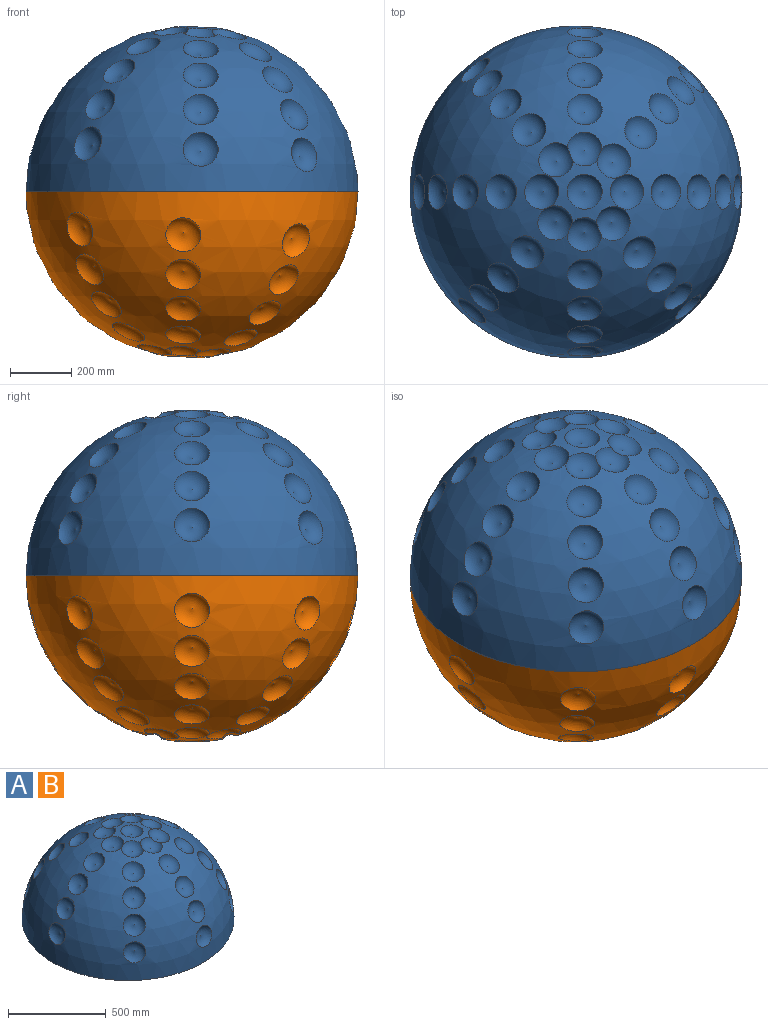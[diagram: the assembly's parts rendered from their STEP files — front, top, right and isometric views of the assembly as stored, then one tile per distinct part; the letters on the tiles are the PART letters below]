
ASSEMBLY  parts=2 mates=1
PART A: 43 faces, bbox 1084.6x1084.6x541.6 mm
  f0: torus R=13.96mm, axis (-0.61,0.74,0.29), area 12860.7mm2, adj f21
  f1: torus R=13.96mm, axis (-0.54,0.66,0.53), area 12860.7mm2, adj f21
  f2: torus R=13.96mm, axis (-0.43,0.53,0.73), area 12860.7mm2, adj f21
  f3: torus R=13.96mm, axis (-0.28,0.38,0.88), area 12860.7mm2, adj f21
  f4: torus R=13.96mm, axis (-0.12,0.19,0.97), area 12384.9mm2, adj f15,f21
  f5: torus R=13.96mm, axis (0.22,-0.19,0.96), area 12358.3mm2, adj f14,f21,f28
  f6: torus R=13.96mm, axis (0.38,-0.37,0.85), area 12860.7mm2, adj f21
  f7: torus R=13.96mm, axis (0.52,-0.52,0.68), area 12860.7mm2, adj f21
  f8: torus R=13.96mm, axis (0.62,-0.63,0.47), area 12860.7mm2, adj f21
  f9: torus R=13.96mm, axis (0.68,-0.7,0.22), area 12860.7mm2, adj f21
  f10: torus R=13.96mm, axis (0.05,-0.96,0.26), area 12860.7mm2, adj f21
  f11: torus R=13.96mm, axis (0.05,-0.86,0.5), area 12860.7mm2, adj f21
  f12: torus R=13.96mm, axis (0.05,-0.71,0.71), area 12860.7mm2, adj f21
  f13: torus R=13.96mm, axis (0.05,-0.5,0.86), area 12860.7mm2, adj f21
  f14: torus R=13.96mm, axis (0.05,-0.26,0.96), area 12051.8mm2, adj f5,f21,f37
  f15: torus R=13.96mm, axis (0.05,0.26,0.96), area 12052.1mm2, adj f4,f21,f38
  f16: torus R=13.96mm, axis (0.05,0.5,0.86), area 12860.7mm2, adj f21
  f17: torus R=13.96mm, axis (0.05,0.71,0.71), area 12860.7mm2, adj f21
  f18: torus R=13.96mm, axis (0.05,0.86,0.5), area 12860.7mm2, adj f21
  f19: torus R=13.96mm, axis (0.05,0.96,0.26), area 12860.7mm2, adj f21
  f20: plane 1084.58x1084.58mm, normal (0,0,-1), area 923874.7mm2, adj f21
  f21: sphere r=542.29mm, area 1428860.3mm2, adj f0,f1,f2,f3,f4,f5,f6,f7
  f22: torus R=13.96mm, axis (0.05,0,1), area 12860.7mm2, adj f21
  f23: torus R=13.96mm, axis (-0.95,0,0.31), area 12860.7mm2, adj f21
  f24: torus R=13.96mm, axis (-0.84,0,0.54), area 12860.7mm2, adj f21
  f25: torus R=13.96mm, axis (-0.67,0,0.74), area 12860.7mm2, adj f21
  f26: torus R=13.96mm, axis (-0.45,0,0.89), area 12860.7mm2, adj f21
  f27: torus R=13.96mm, axis (-0.21,0,0.98), area 12806.7mm2, adj f21,f37
  f28: torus R=13.96mm, axis (0.31,0,0.95), area 12763.2mm2, adj f5,f21,f38
  f29: torus R=13.96mm, axis (0.54,0,0.84), area 12860.7mm2, adj f21
  f30: torus R=13.96mm, axis (0.74,0,0.67), area 12860.7mm2, adj f21
  f31: torus R=13.96mm, axis (0.89,0,0.45), area 12860.7mm2, adj f21
  f32: torus R=13.96mm, axis (0.98,0,0.21), area 12860.7mm2, adj f21
  f33: torus R=13.96mm, axis (-0.63,-0.72,0.29), area 12860.7mm2, adj f21
  f34: torus R=13.96mm, axis (-0.56,-0.64,0.53), area 12860.7mm2, adj f21
  f35: torus R=13.96mm, axis (-0.44,-0.52,0.73), area 12860.7mm2, adj f21
  f36: torus R=13.96mm, axis (-0.29,-0.37,0.88), area 12860.7mm2, adj f21
  f37: torus R=13.96mm, axis (-0.13,-0.19,0.97), area 12495.3mm2, adj f14,f21,f27
  f38: torus R=13.96mm, axis (0.23,0.19,0.96), area 12435.2mm2, adj f15,f21,f28
  f39: torus R=13.96mm, axis (0.39,0.36,0.85), area 12860.7mm2, adj f21
  f40: torus R=13.96mm, axis (0.53,0.5,0.68), area 12860.7mm2, adj f21
  f41: torus R=13.96mm, axis (0.64,0.61,0.47), area 12860.7mm2, adj f21
  f42: torus R=13.96mm, axis (0.7,0.68,0.22), area 12860.7mm2, adj f21
PART B: same geometry as A
PLACE A t=(674.96,-630.18,754.69)mm
PLACE B rot(axis=(0,1,0),180deg) t=(674.96,-630.18,754.69)mm
MATE fastened B.f20 <-> A.f20  axis (0,0,-1) through (674.96,-630.18,754.69)mm
